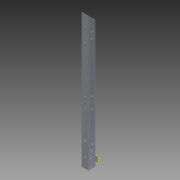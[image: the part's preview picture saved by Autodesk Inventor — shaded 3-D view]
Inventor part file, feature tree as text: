
AUTODESK INVENTOR PART (.ipt)
format: ipt  version: 2013 (Build 170138000, 138)  size: 160,768 bytes
history: native  units: in
note: dims shown in document units (in); Inventor stores cm internally (conversion verified against a paired STEP export)
features: extrude x11, sketch x10, reference x10, plane x1
ambient origin geometry x8: Origin, YZ Plane, XZ Plane, XY Plane, X Axis, Y Axis, Z Axis, Center Point
bodies: Solid1 (feature_tree)
feature tree (32):
  extrude  "Extrusion1"  Depth=1.0in
  extrude  "Extrusion3"  Depth=19.5in TaperAngle=0.0deg
  plane  "Work Plane1"
  extrude  "Extrusion4"  Depth=0.266in
  extrude  "Extrusion5"  Depth=1.5in
  extrude  "Extrusion6"  Depth=0.25in
  extrude  "Extrusion9"  Depth=0.266in
  extrude  "Extrusion10"  Depth=2.5in
  extrude  "Extrusion11"  Depth=0.25in
  extrude  "Extrusion12"  Depth=1.0in TaperAngle=0.0deg
  extrude  "Extrusion13"  Depth=1.0in TaperAngle=0.0deg
  extrude  "Extrusion14"  Depth=1.0in TaperAngle=0.0deg
  sketch  "Sketch1"  dims[d0=1.0in d2=1.0in]
  sketch  "Sketch3"  dims[d3=0.875in d4=19.5in d5=0.0in]
  sketch  "Sketch4"  dims[d7=45.0deg d10=0.266in]
  sketch  "Sketch5"  dims[d11=0.266in d12=1.5in]
  reference  "Reference3"
  reference  "Reference4"
  sketch  "Sketch8"  dims[d13=0.25in d14=0.25in]
  reference  "Reference12"
  reference  "Reference13"
  reference  "Reference14"
  reference  "Reference15"
  sketch  "Sketch9"  dims[d15=2.5in d16=0.266in]
  reference  "Reference16"
  reference  "Reference17"
  reference  "Reference18"
  reference  "Reference19"
  sketch  "Sketch10"  dims[d17=0.266in d18=2.5in]
  sketch  "Sketch11"  dims[d19=1.5in d20=0.25in]
  sketch  "Sketch12"  dims[d21=0.25in d22=1.0in d23=0.0in]
  sketch  "Sketch13"  dims[d24=1.0in d25=0.0in d26=1.0in d27=0.0in d28=1.0in d29=0.0in d34=1.0in d35=0.0in d36=1.0in d37=0.0in d38=0.0625in d39=0.0in d40=0.0625in d41=0.0in d42=0.0625in d43=0.0in d44=0.0625in d45=0.0in]
